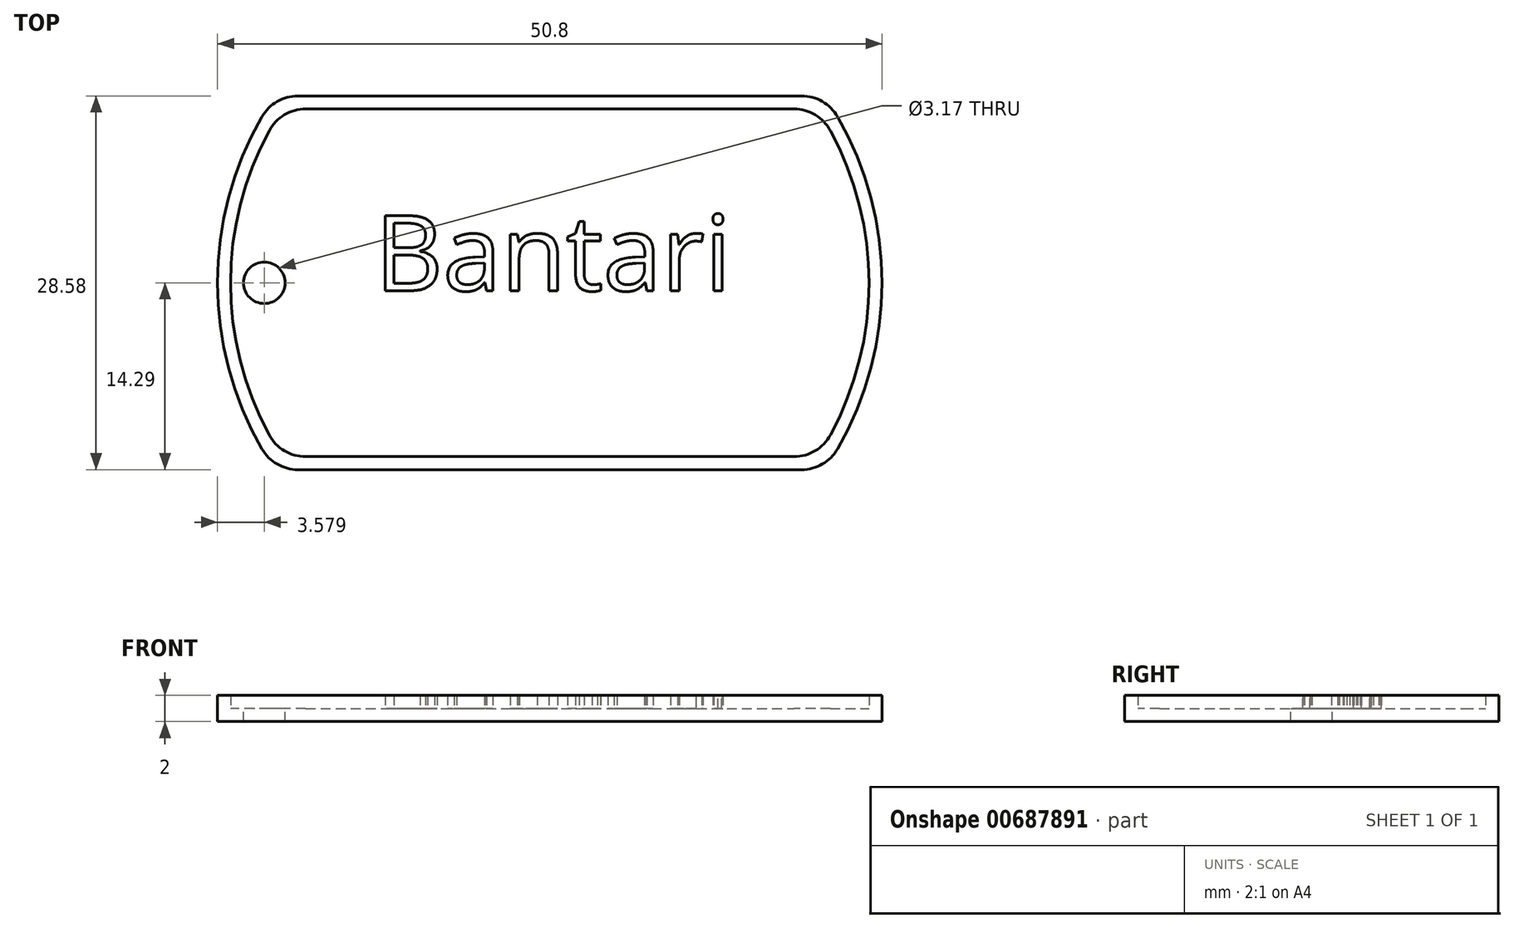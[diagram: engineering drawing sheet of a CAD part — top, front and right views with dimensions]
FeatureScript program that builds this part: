
annotation { "Feature Type Name" : "Feature", "Feature Type Description" : "" }
export const myFeature = defineFeature(function(context is Context, id is Id, definition is map)
    precondition{}
    {
        {
            var Q0;
            Q0=qCreatedBy(makeId("Top.planeOp"),FACE);
            var sketch = newSketch(context, id + "F0", { "sketchPlane" : qUnion([Q0])});
            skArc(sketch, "E0", {"start": v(-22, 12.7) * mm, "mid": v(-25.4, 0) * mm, "end": v(-22, -12.7) * mm});
            skLineSegment(sketch, "E1.top", {"start": v(-19.25, -14.29) * mm, "end": v(19.25, -14.29) * mm});
            skArc(sketch, "E2.trimOffspring", {"start": v(22, -12.7) * mm, "mid": v(25.4, 0) * mm, "end": v(22, 12.7) * mm});
            skLineSegment(sketch, "E3", {"start": v(-19.25, 14.29) * mm, "end": v(19.25, 14.29) * mm});
            skPoint(sketch, "E4.visualSharp", {"position": v(-21, 14.29) * mm});
            skArc(sketch, "E4.filletArc", {"start": v(-19.25, 14.29) * mm, "mid": v(-20.83, 13.86) * mm, "end": v(-22, 12.7) * mm});
            skPoint(sketch, "E5.visualSharp", {"position": v(21, 14.29) * mm});
            skArc(sketch, "E5.filletArc", {"start": v(22, 12.7) * mm, "mid": v(20.83, 13.86) * mm, "end": v(19.25, 14.29) * mm});
            skPoint(sketch, "E6.visualSharp", {"position": v(21, -14.29) * mm});
            skArc(sketch, "E6.filletArc", {"start": v(19.25, -14.29) * mm, "mid": v(20.83, -13.86) * mm, "end": v(22, -12.7) * mm});
            skPoint(sketch, "E7.visualSharp", {"position": v(-21, -14.29) * mm});
            skArc(sketch, "E7.filletArc", {"start": v(-22, -12.7) * mm, "mid": v(-20.83, -13.86) * mm, "end": v(-19.25, -14.29) * mm});
            skSolve(sketch);
        }
        {
            var Q0;
            Q0=makeQuery(id+"F0.imprint","IMPRINT",FACE,{"disambiguationData":[TD([[makeQuery(id+"F0.imprint","IMPRINT",EDGE,{"derivedFrom":sQuery(id+"F0.wireOp",EDGE,"E0")}),1.0]])]});
            extrude(context, id + "F1", {"entities" : qUnion([Q0]), "depth" : 1 * mm, "offsetDistance" : 25.4 * mm});
        }
        {
            var Q0;
            Q0=makeQuery(id+"F1.opExtrude","CAP_FACE",FACE,{"disambiguationData":[OSD([sQuery(id+"F0.wireOp",EDGE,"E0"),sQuery(id+"F0.wireOp",EDGE,"E1.top"),sQuery(id+"F0.wireOp",EDGE,"E2.trimOffspring"),sQuery(id+"F0.wireOp",EDGE,"E3"),sQuery(id+"F0.wireOp",EDGE,"E4.filletArc"),sQuery(id+"F0.wireOp",EDGE,"E5.filletArc"),sQuery(id+"F0.wireOp",EDGE,"E6.filletArc"),sQuery(id+"F0.wireOp",EDGE,"E7.filletArc")])],"isStart":false});
            var sketch = newSketch(context, id + "F2", { "sketchPlane" : qUnion([Q0])});
            skLineSegment(sketch, "E8.0", {"start": v(-18.66, 13.29) * mm, "end": v(18.66, 13.29) * mm});
            skArc(sketch, "E8.1", {"start": v(-21.45, 11.63) * mm, "mid": v(-24.4, 0) * mm, "end": v(-21.45, -11.63) * mm});
            skLineSegment(sketch, "E8.2", {"start": v(-18.66, -13.29) * mm, "end": v(18.66, -13.29) * mm});
            skArc(sketch, "E8.3", {"start": v(21.45, -11.63) * mm, "mid": v(24.4, 0) * mm, "end": v(21.45, 11.63) * mm});
            skPoint(sketch, "E9.visualSharp", {"position": v(-20.46, 13.29) * mm});
            skArc(sketch, "E9.filletArc", {"start": v(-18.66, 13.29) * mm, "mid": v(-20.29, 12.84) * mm, "end": v(-21.45, 11.63) * mm});
            skPoint(sketch, "E10.visualSharp", {"position": v(20.46, 13.29) * mm});
            skArc(sketch, "E10.filletArc", {"start": v(21.45, 11.63) * mm, "mid": v(20.29, 12.84) * mm, "end": v(18.66, 13.29) * mm});
            skPoint(sketch, "E11.visualSharp", {"position": v(20.46, -13.29) * mm});
            skArc(sketch, "E11.filletArc", {"start": v(18.66, -13.29) * mm, "mid": v(20.29, -12.84) * mm, "end": v(21.45, -11.63) * mm});
            skPoint(sketch, "E12.visualSharp", {"position": v(-20.46, -13.29) * mm});
            skArc(sketch, "E12.filletArc", {"start": v(-21.45, -11.63) * mm, "mid": v(-20.29, -12.84) * mm, "end": v(-18.66, -13.29) * mm});
            skLineSegment(sketch, "E13.0", {"start": v(-19.25, 14.29) * mm, "end": v(19.25, 14.29) * mm});
            skArc(sketch, "E13.1", {"start": v(-22, 12.7) * mm, "mid": v(-25.4, 0) * mm, "end": v(-22, -12.7) * mm});
            skLineSegment(sketch, "E13.2", {"start": v(-19.25, -14.29) * mm, "end": v(19.25, -14.29) * mm});
            skArc(sketch, "E13.3", {"start": v(22, -12.7) * mm, "mid": v(25.4, 0) * mm, "end": v(22, 12.7) * mm});
            skPoint(sketch, "E14.visualSharp", {"position": v(-21, -14.29) * mm});
            skArc(sketch, "E14.filletArc", {"start": v(-22, -12.7) * mm, "mid": v(-20.83, -13.86) * mm, "end": v(-19.25, -14.29) * mm});
            skPoint(sketch, "E15.visualSharp", {"position": v(21, -14.29) * mm});
            skArc(sketch, "E15.filletArc", {"start": v(19.25, -14.29) * mm, "mid": v(20.83, -13.86) * mm, "end": v(22, -12.7) * mm});
            skPoint(sketch, "E16.visualSharp", {"position": v(21, 14.29) * mm});
            skArc(sketch, "E16.filletArc", {"start": v(22, 12.7) * mm, "mid": v(20.83, 13.86) * mm, "end": v(19.25, 14.29) * mm});
            skPoint(sketch, "E17.visualSharp", {"position": v(-21, 14.29) * mm});
            skArc(sketch, "E17.filletArc", {"start": v(-19.25, 14.29) * mm, "mid": v(-20.83, 13.86) * mm, "end": v(-22, 12.7) * mm});
            skSolve(sketch);
        }
        {
            var Q0;
            Q0=makeQuery(id+"F2.imprint","IMPRINT",FACE,{"disambiguationData":[TD([[makeQuery(id+"F2.imprint","IMPRINT",EDGE,{"derivedFrom":sQuery(id+"F2.wireOp",EDGE,"E8.0")}),1.0]])]});
            extrude(context, id + "F3", {"entities" : qUnion([Q0]), "operationType" : NewBodyOperationType.ADD, "depth" : 1 * mm, "offsetDistance" : 25.4 * mm});
        }
        {
            var Q0;
            Q0=makeQuery(id+"F1.opExtrude","CAP_FACE",FACE,{"disambiguationData":[OSD([sQuery(id+"F0.wireOp",EDGE,"E0"),sQuery(id+"F0.wireOp",EDGE,"E1.top"),sQuery(id+"F0.wireOp",EDGE,"E2.trimOffspring"),sQuery(id+"F0.wireOp",EDGE,"E3"),sQuery(id+"F0.wireOp",EDGE,"E4.filletArc"),sQuery(id+"F0.wireOp",EDGE,"E5.filletArc"),sQuery(id+"F0.wireOp",EDGE,"E6.filletArc"),sQuery(id+"F0.wireOp",EDGE,"E7.filletArc")])],"isStart":false});
            var sketch = newSketch(context, id + "F4", { "sketchPlane" : qUnion([Q0])});
            skCircle(sketch, "E18", {"center": v(-21.82, 0) * mm, "radius": 1.59 * mm});
            skSolve(sketch);
        }
        {
            var Q0;
            Q0=makeQuery(id+"F4.imprint","IMPRINT",FACE,{"disambiguationData":[TD([[makeQuery(id+"F4.imprint","IMPRINT",EDGE,{"derivedFrom":sQuery(id+"F4.wireOp",EDGE,"E18")}),1.0]])]});
            extrude(context, id + "F5", {"entities" : qUnion([Q0]), "operationType" : NewBodyOperationType.REMOVE, "oppositeDirection" : true, "depth" : 1 * mm, "offsetDistance" : 25.4 * mm});
        }
        {
            var Q0;
            Q0=makeQuery(id+"F2.imprint","IMPRINT",FACE,{"disambiguationData":[TD([[makeQuery(id+"F2.imprint","IMPRINT",EDGE,{"derivedFrom":sQuery(id+"F2.wireOp",EDGE,"E8.0")}),-1.0]])]});
            var sketch = newSketch(context, id + "F6", { "sketchPlane" : qUnion([Q0])});
            skText(sketch, "E19", { "text": "Bantari", "fontName": "OpenSans-Regular.ttf"});
            const initialGuessF6  = {"E19": [-0.01338, -0.0006, 1, 0, 0.00579]};
            skSetInitialGuess(sketch, initialGuessF6);
            skSolve(sketch);
        }
        {
            var Q0;
            Q0 = qSketchRegion(id + "F6", true);
            extrude(context, id + "F7", {"entities" : qUnion([Q0]), "operationType" : NewBodyOperationType.ADD, "depth" : 1 * mm, "offsetDistance" : 25.4 * mm});
        }
    });
